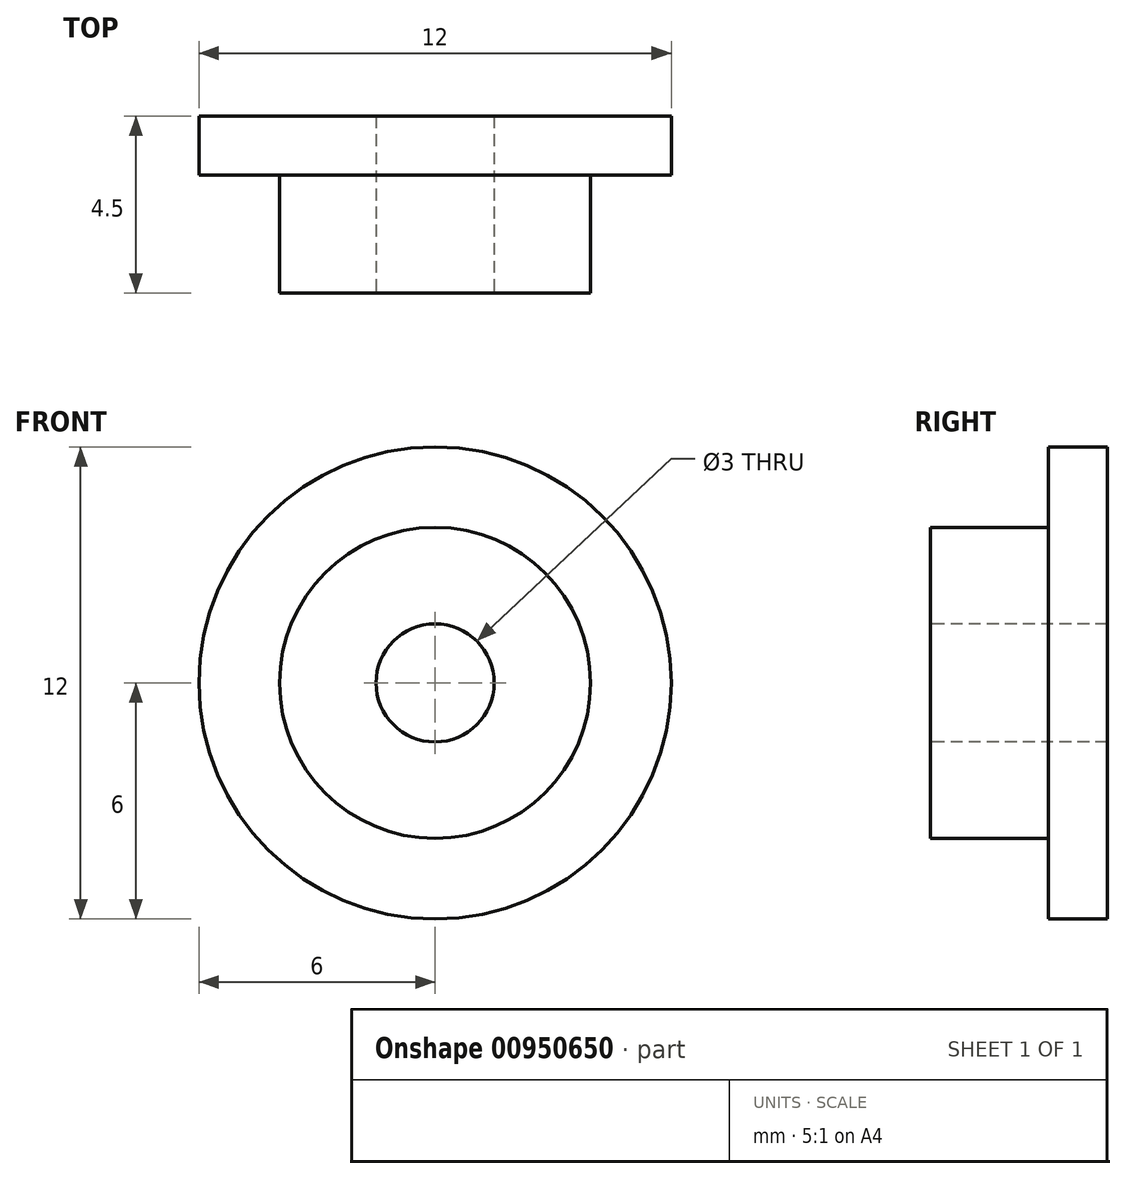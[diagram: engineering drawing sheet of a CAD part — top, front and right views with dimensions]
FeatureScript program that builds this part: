
annotation { "Feature Type Name" : "Feature", "Feature Type Description" : "" }
export const myFeature = defineFeature(function(context is Context, id is Id, definition is map)
    precondition{}
    {
        {
            var Q0;
            Q0=qCreatedBy(makeId("Front.planeOp"),FACE);
            var sketch = newSketch(context, id + "F0", { "sketchPlane" : qUnion([Q0])});
            skCircle(sketch, "E0", {"center": v(0, 0) * mm, "radius": 6 * mm});
            skPoint(sketch, "E1", {"position": v(0.83, 2.66) * mm});
            skPoint(sketch, "E2", {"position": v(1.89, 1.7) * mm});
            skSolve(sketch);
        }
        {
            var Q0;
            Q0=makeQuery(id+"F0.imprint","IMPRINT",FACE,{"disambiguationData":[TD([[makeQuery(id+"F0.imprint","IMPRINT",EDGE,{"derivedFrom":sQuery(id+"F0.wireOp",EDGE,"E0")}),1.0]])]});
            extrude(context, id + "F1", {"entities" : qUnion([Q0]), "depth" : 1.5 * mm, "offsetDistance" : 25 * mm});
        }
        {
            var Q0;
            Q0=makeQuery(id+"F1.opExtrude","CAP_FACE",FACE,{"disambiguationData":[OSD([sQuery(id+"F0.wireOp",EDGE,"E0")])],"isStart":false});
            var sketch = newSketch(context, id + "F2", { "sketchPlane" : qUnion([Q0])});
            skCircle(sketch, "E3", {"center": v(0, 0) * mm, "radius": 3.95 * mm});
            skPoint(sketch, "E4", {"position": v(0.18, 1.16) * mm});
            skSolve(sketch);
        }
        {
            var Q0;
            Q0=makeQuery(id+"F2.imprint","IMPRINT",FACE,{"disambiguationData":[TD([[makeQuery(id+"F2.imprint","IMPRINT",EDGE,{"derivedFrom":sQuery(id+"F2.wireOp",EDGE,"E3")}),1.0]])]});
            extrude(context, id + "F3", {"entities" : qUnion([Q0]), "operationType" : NewBodyOperationType.ADD, "depth" : 3 * mm, "offsetDistance" : 25 * mm});
        }
        {
            var Q0;
            Q0=makeQuery(id+"F3.opExtrude","CAP_FACE",FACE,{"disambiguationData":[OSD([sQuery(id+"F2.wireOp",EDGE,"E3")])],"isStart":false});
            var sketch = newSketch(context, id + "F4", { "sketchPlane" : qUnion([Q0])});
            skPoint(sketch, "E5", {"position": v(0, 0) * mm});
            skSolve(sketch);
        }
        {
            var Q0;
            Q0=sQuery(id+"F4.wireOp",VERTEX,"E5");
            var Q1;
            Q1=makeQuery(id+"F1.opExtrude","SWEPT_BODY",BODY,{"disambiguationData":[OSD([sQuery(id+"F0.wireOp",EDGE,"E0")])]});
            hole(context, id + "F5", {"style" : HoleStyle.SIMPLE, "endStyle" : HoleEndStyle.THROUGH, "holeDiameter" : 3 * mm, "majorDiameter" : 5 * mm, "isTappedThrough" : true, "tappedDepth" : 12 * mm, "tapClearance" : 3, "locations" : qUnion([Q0]), "scope" : qUnion([Q1])});
        }
    });
